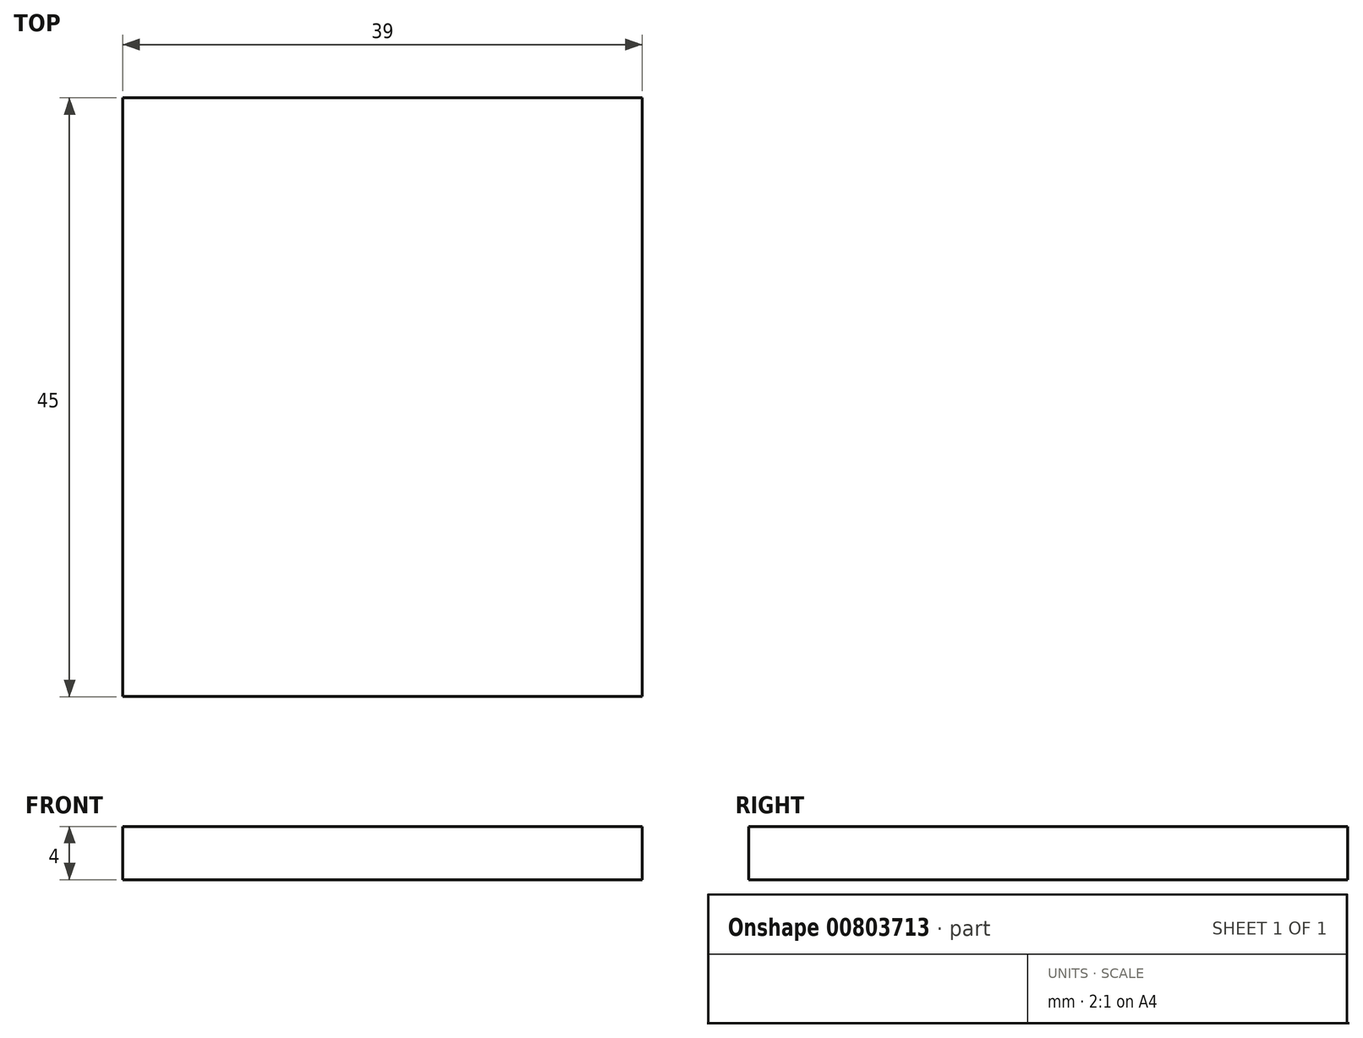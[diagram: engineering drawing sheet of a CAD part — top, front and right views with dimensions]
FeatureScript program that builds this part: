
annotation { "Feature Type Name" : "Feature", "Feature Type Description" : "" }
export const myFeature = defineFeature(function(context is Context, id is Id, definition is map)
    precondition{}
    {
        {
            var Q0;
            Q0=qCreatedBy(makeId("Top.planeOp"),FACE);
            var sketch = newSketch(context, id + "F0", { "sketchPlane" : qUnion([Q0])});
            skLineSegment(sketch, "E0.bottom", {"start": v(-21.15, 28.25) * mm, "end": v(17.85, 28.25) * mm});
            skLineSegment(sketch, "E0.top", {"start": v(-21.15, -16.75) * mm, "end": v(17.85, -16.75) * mm});
            skLineSegment(sketch, "E0.left", {"start": v(-21.15, 28.25) * mm, "end": v(-21.15, -16.75) * mm});
            skLineSegment(sketch, "E0.right", {"start": v(17.85, 28.25) * mm, "end": v(17.85, -16.75) * mm});
            skSolve(sketch);
        }
        {
            var Q0;
            Q0 = qSketchRegion(id + "F0", true);
            extrude(context, id + "F1", {"entities" : qUnion([Q0]), "depth" : 4 * mm, "offsetDistance" : 25 * mm});
        }
    });
